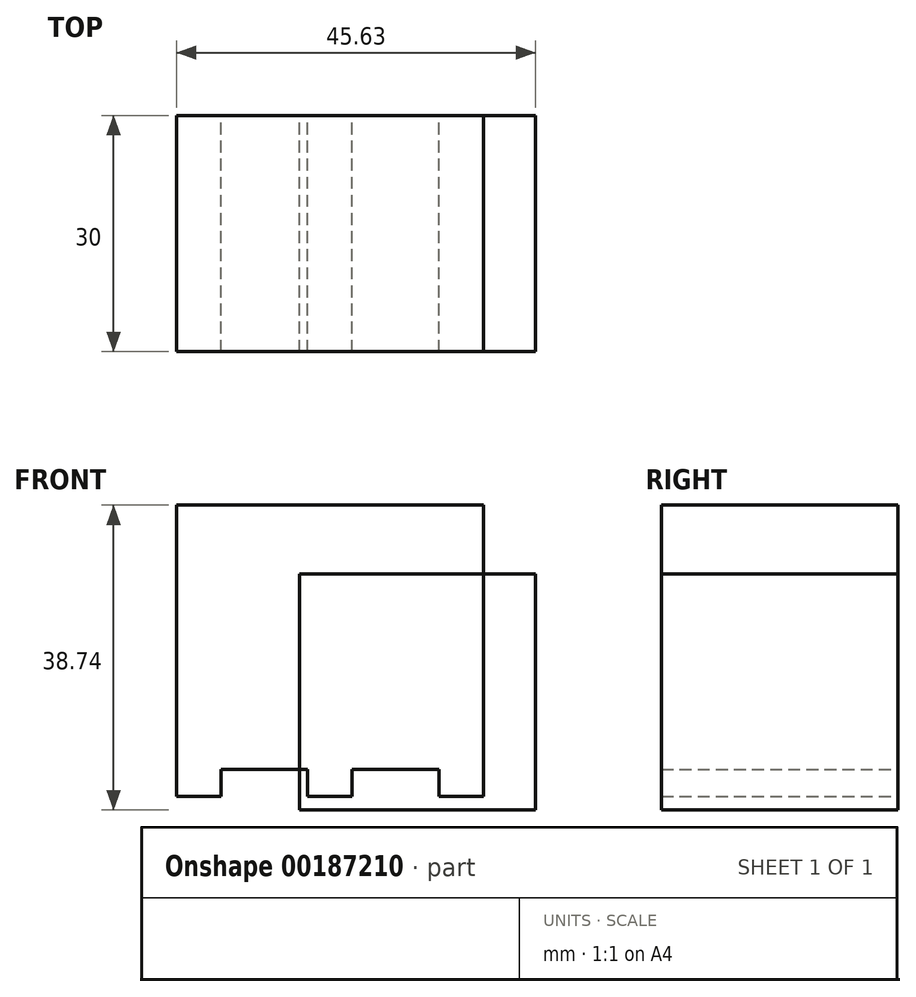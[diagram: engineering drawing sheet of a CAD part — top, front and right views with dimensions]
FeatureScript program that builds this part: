
annotation { "Feature Type Name" : "Feature", "Feature Type Description" : "" }
export const myFeature = defineFeature(function(context is Context, id is Id, definition is map)
    precondition{}
    {
        {
            var Q0;
            Q0=qCreatedBy(makeId("Front.planeOp"),FACE);
            var sketch = newSketch(context, id + "F0", { "sketchPlane" : qUnion([Q0])});
            skLineSegment(sketch, "E0", {"start": v(-56.3, 16.2) * mm, "end": v(-56.3, 53.2) * mm});
            skLineSegment(sketch, "E1", {"start": v(-56.3, 53.2) * mm, "end": v(-17.3, 53.2) * mm});
            skLineSegment(sketch, "E2", {"start": v(-17.3, 53.2) * mm, "end": v(-17.3, 16.2) * mm});
            skLineSegment(sketch, "E3", {"start": v(-36.8, 53.2) * mm, "end": v(-36.8, 16.2) * mm, "construction": true});
            skLineSegment(sketch, "E4", {"start": v(-39.62, 16.2) * mm, "end": v(-33.96, 16.2) * mm});
            skLineSegment(sketch, "E5", {"start": v(-39.62, 16.2) * mm, "end": v(-39.62, 19.64) * mm});
            skLineSegment(sketch, "E6", {"start": v(-39.62, 19.64) * mm, "end": v(-50.62, 19.64) * mm});
            skLineSegment(sketch, "E7", {"start": v(-50.62, 19.64) * mm, "end": v(-50.62, 16.2) * mm});
            skLineSegment(sketch, "E8", {"start": v(-50.62, 16.2) * mm, "end": v(-56.3, 16.2) * mm});
            skLineSegment(sketch, "E9", {"start": v(-33.96, 16.2) * mm, "end": v(-33.96, 19.64) * mm});
            skLineSegment(sketch, "E10", {"start": v(-33.96, 19.64) * mm, "end": v(-22.96, 19.64) * mm});
            skLineSegment(sketch, "E11", {"start": v(-22.96, 19.64) * mm, "end": v(-22.96, 16.2) * mm});
            skLineSegment(sketch, "E12", {"start": v(-22.96, 16.2) * mm, "end": v(-17.3, 16.2) * mm});
            skSolve(sketch);
        }
        {
            var Q0;
            Q0 = qSketchRegion(id + "F0", true);
            extrude(context, id + "F1", {"entities" : qUnion([Q0]), "depth" : 30 * mm});
        }
        {
            var Q0;
            Q0=qCreatedBy(makeId("Front.planeOp"),FACE);
            var sketch = newSketch(context, id + "F2", { "sketchPlane" : qUnion([Q0])});
            skLineSegment(sketch, "E13.bottom", {"start": v(-40.66, 14.45) * mm, "end": v(-10.66, 14.45) * mm});
            skLineSegment(sketch, "E13.top", {"start": v(-40.66, 44.45) * mm, "end": v(-10.66, 44.45) * mm});
            skLineSegment(sketch, "E13.left", {"start": v(-40.66, 14.45) * mm, "end": v(-40.66, 44.45) * mm});
            skLineSegment(sketch, "E13.right", {"start": v(-10.66, 14.45) * mm, "end": v(-10.66, 44.45) * mm});
            skSolve(sketch);
        }
        {
            var Q0;
            Q0 = qSketchRegion(id + "F2", true);
            extrude(context, id + "F3", {"entities" : qUnion([Q0]), "depth" : 30 * mm});
        }
    });
